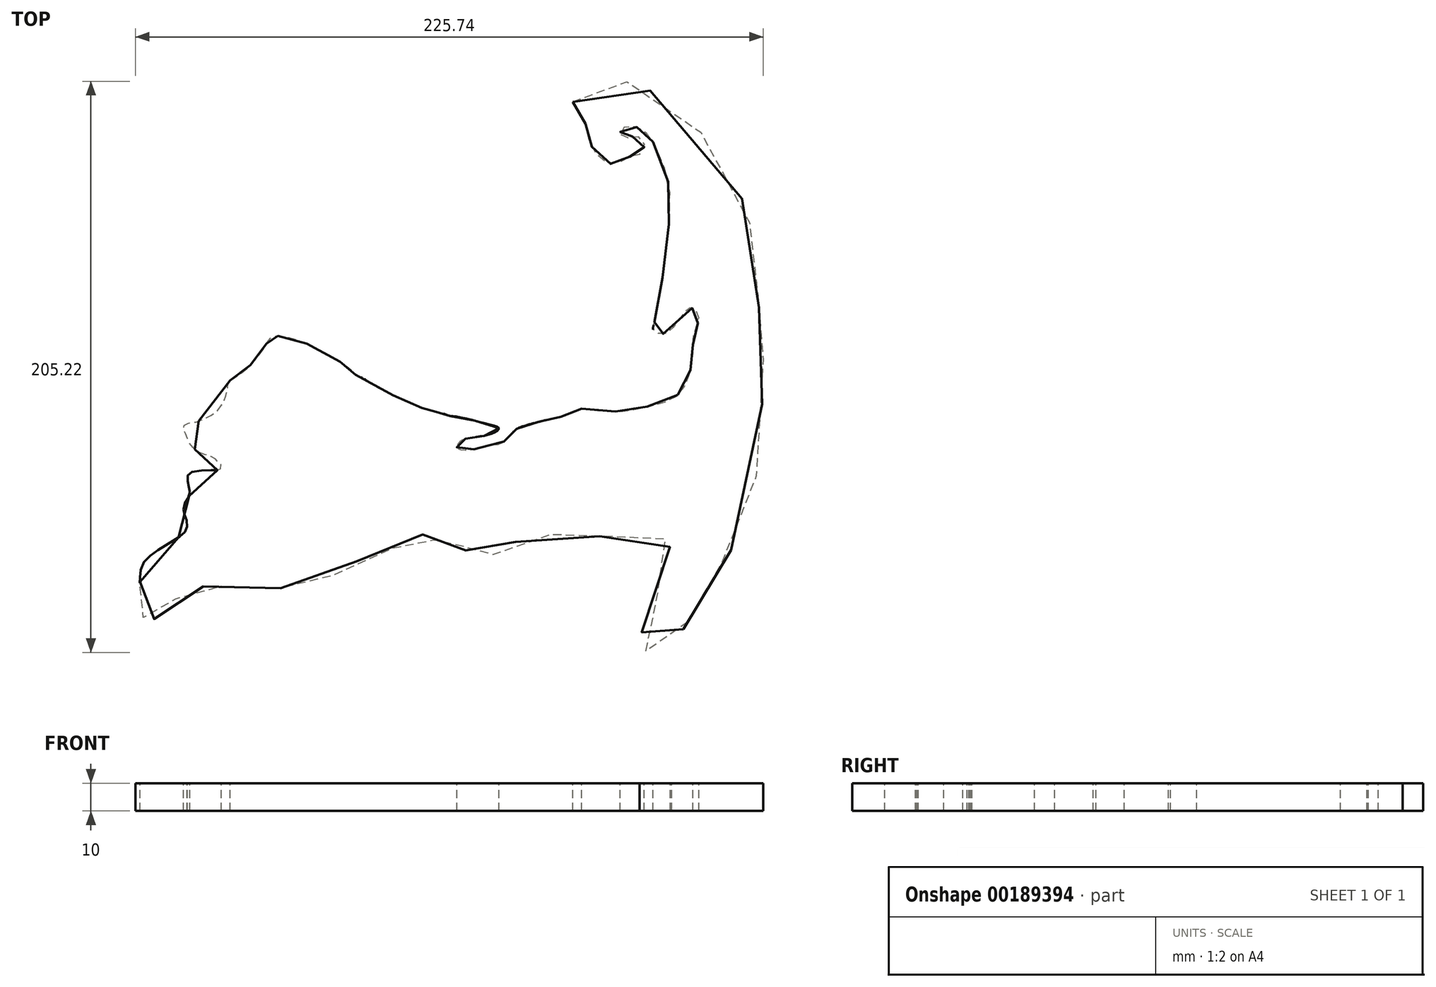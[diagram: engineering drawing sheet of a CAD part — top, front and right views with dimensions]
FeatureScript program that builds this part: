
annotation { "Feature Type Name" : "Feature", "Feature Type Description" : "" }
export const myFeature = defineFeature(function(context is Context, id is Id, definition is map)
    precondition{}
    {
        {
            var Q0;
            Q0=qCreatedBy(makeId("Top.planeOp"),FACE);
            var sketch = newSketch(context, id + "F0", { "sketchPlane" : qUnion([Q0])});
            skLineSegment(sketch, "E0.bottom", {"start": v(114, -114) * mm, "end": v(-114, -114) * mm});
            skLineSegment(sketch, "E0.top", {"start": v(114, 114) * mm, "end": v(-114, 114) * mm});
            skLineSegment(sketch, "E0.left", {"start": v(114, -114) * mm, "end": v(114, 114) * mm});
            skLineSegment(sketch, "E0.right", {"start": v(-114, -114) * mm, "end": v(-114, 114) * mm});
            skPoint(sketch, "E0.middle", {"position": v(0, 0) * mm});
            skSolve(sketch);
        }
        {
            var Q0;
            Q0 = qSketchRegion(id + "F0", true);
            extrude(context, id + "F1", {"entities" : qUnion([Q0]), "depth" : 10 * mm});
        }
        {
            var Q0;
            Q0=makeQuery(id+"F1.opExtrude","CAP_FACE",FACE,{"disambiguationData":[OSD([sQuery(id+"F0.wireOp",EDGE,"E0.bottom"),sQuery(id+"F0.wireOp",EDGE,"E0.top"),sQuery(id+"F0.wireOp",EDGE,"E0.left"),sQuery(id+"F0.wireOp",EDGE,"E0.right")])],"isStart":false});
            var sketch = newSketch(context, id + "F2", { "sketchPlane" : qUnion([Q0])});
            skFitSpline(sketch, "E1", {"points": [v(-78.88, -5.08) * mm, v(-71.93, 0) * mm, v(-65.75, 8.04) * mm, v(-64.34, 10.1) * mm, v(-60.22, 10.76) * mm, v(-45.46, 5.22) * mm, v(-34.6, -2.05) * mm, v(-33.63, -3.24) * mm, v(-31.03, -4.32) * mm, v(-28.86, -5.84) * mm, v(-15.5, -12.68) * mm, v(-8.2, -15.6) * mm, v(-6.75, -15.96) * mm, v(-1.36, -17.33) * mm, v(0, -17.85) * mm, v(1.56, -17.97) * mm, v(14.91, -21.12) * mm, v(17.78, -22.45) * mm, v(15.22, -24.3) * mm, v(8.77, -25.52) * mm, v(5.29, -26.24) * mm, v(3.24, -27.67) * mm, v(2.73, -29.3) * mm, v(5.6, -30.13) * mm, v(11.84, -29.1) * mm, v(13.58, -28.5) * mm, v(15.83, -28.39) * mm, v(19.62, -27.06) * mm, v(23.2, -23.37) * mm, v(26.07, -21.73) * mm, v(36, -19.07) * mm, v(40.82, -18.04) * mm, v(47.56, -15.3) * mm], "startDerivative": vector(166.8, 100.66) * mm, "endDerivative": vector(189.52, 84.83) * mm});
            skFitSpline(sketch, "E2", {"points": [v(47.56, -15.3) * mm, v(57.46, -16.2) * mm, v(64.01, -15.98) * mm, v(73.61, -13.96) * mm, v(81.31, -10.98) * mm, v(85.16, -5.8) * mm, v(86.95, 0) * mm, v(87.53, 5.77) * mm, v(87.53, 9.4) * mm, v(88.54, 13.6) * mm, v(89.7, 16.63) * mm, v(89.12, 19.38) * mm, v(87.38, 20.83) * mm, v(85.65, 20.69) * mm, v(84.05, 18.66) * mm, v(81.3, 15.04) * mm, v(78.55, 12) * mm, v(75.65, 11.7) * mm, v(73.33, 12.72) * mm, v(73.62, 15.62) * mm, v(76.53, 31.15) * mm, v(79.11, 53.37) * mm, v(78.42, 67.32) * mm, v(73.08, 80.75) * mm, v(70.48, 84.05) * mm, v(67.39, 85.9) * mm, v(63.32, 86.06) * mm, v(61.58, 84.97) * mm, v(61.58, 83.24) * mm, v(62.94, 82.15) * mm, v(64.73, 82.31) * mm, v(67.44, 82.58) * mm, v(69.56, 81.23) * mm, v(69.88, 78.24) * mm, v(67.71, 75.7) * mm, v(65.22, 75.42) * mm, v(63.75, 74.61) * mm, v(59.8, 72.77) * mm, v(56.1, 73.3) * mm, v(52.04, 77.21) * mm, v(49.95, 82.77) * mm, v(49.22, 86.1) * mm, v(46.4, 91.9) * mm, v(44.37, 95) * mm], "startDerivative": vector(310, -33.18) * mm, "endDerivative": vector(-90.92, 130.97) * mm});
            skFitSpline(sketch, "E3", {"points": [v(44.37, 95) * mm, v(45.92, 98.47) * mm, v(56.68, 101.95) * mm, v(66.4, 101.65) * mm, v(79.82, 93.66) * mm, v(99.15, 72.93) * mm, v(107.62, 52.53) * mm, v(109.79, 42.33) * mm, v(111.09, 24.46) * mm, v(111.8, 13.57) * mm, v(112.6, 9.88) * mm, v(112.77, 1.47) * mm, v(111.47, -28.99) * mm, v(106, -56.9) * mm, v(97.6, -71.32) * mm, v(91.81, -79.16) * mm, v(86.39, -89.58) * mm, v(82.91, -96.3) * mm, v(77.27, -101.3) * mm, v(72.06, -102.82) * mm, v(68.8, -100.86) * mm, v(68.8, -96.74) * mm, v(73.58, -85.02) * mm, v(78.57, -73.74) * mm, v(79.88, -67.88) * mm, v(77.05, -61.59) * mm, v(70.98, -59.85) * mm, v(65.26, -61.39) * mm, v(58.3, -61.24) * mm, v(44.37, -60.95) * mm, v(39.63, -60.52) * mm, v(32.38, -60.95) * mm, v(22.54, -63.7) * mm, v(15.87, -67.47) * mm, v(14.72, -68.92) * mm, v(11.1, -69.93) * mm, v(7.18, -69.2) * mm, v(5.88, -66.17) * mm, v(4.59, -62.86) * mm, v(2.95, -61.03) * mm, v(-0.8, -62.22) * mm, v(-3.44, -63.13) * mm, v(-7.18, -61.58) * mm, v(-13.3, -60.3) * mm, v(-18.95, -63.95) * mm, v(-20.32, -65.41) * mm, v(-27.64, -67.35) * mm, v(-36.39, -71.95) * mm, v(-46.67, -77.78) * mm, v(-53.88, -79.93) * mm, v(-59.4, -79.63) * mm, v(-63.4, -80.09) * mm, v(-70.3, -79.32) * mm, v(-79.81, -79.17) * mm, v(-88, -79.15) * mm, v(-90.9, -79.84) * mm, v(-95.43, -81.9) * mm, v(-100.57, -85.28) * mm, v(-103.95, -88.89) * mm, v(-105.8, -90.65) * mm, v(-108.17, -91.11) * mm, v(-111.09, -89.58) * mm, v(-112.7, -87.35) * mm, v(-112.7, -83.29) * mm, v(-111.78, -79.07) * mm, v(-111.32, -77.84) * mm, v(-111.24, -75.54) * mm, v(-110.32, -71.17) * mm, v(-106.07, -66.97) * mm, v(-101.36, -63.93) * mm, v(-97.05, -61.28) * mm, v(-94.8, -59.04) * mm, v(-94.35, -56.74) * mm, v(-94.92, -53.98) * mm, v(-95.61, -52.09) * mm, v(-95.1, -49.1) * mm, v(-93.84, -47.19) * mm, v(-93.39, -44.41) * mm, v(-93.97, -42.54) * mm, v(-94.16, -40.16) * mm, v(-93.52, -38.41) * mm, v(-87.65, -37.45) * mm, v(-83.71, -37.38) * mm, v(-82.74, -37.25) * mm, v(-81.97, -36.16) * mm, v(-82.49, -34.87) * mm, v(-83.45, -34.22) * mm, v(-84.16, -33.38) * mm, v(-86.1, -32.22) * mm, v(-88.61, -31.58) * mm, v(-91.32, -30.03) * mm, v(-93.65, -27.45) * mm, v(-94.1, -26.1) * mm, v(-94.74, -24.54) * mm, v(-95.52, -23.25) * mm, v(-95.52, -21.7) * mm, v(-94.68, -20.67) * mm, v(-91.34, -20.1) * mm, v(-86.68, -18.25) * mm, v(-82.95, -15.55) * mm, v(-80.36, -10.72) * mm, v(-79.69, -7.26) * mm, v(-79.52, -5.8) * mm, v(-78.88, -5.08) * mm], "startDerivative": vector(72.46, 444.16) * mm, "endDerivative": vector(185.1, 153.17) * mm});
            skLineSegment(sketch, "E4.bottom", {"start": v(135, -135) * mm, "end": v(-135, -135) * mm});
            skLineSegment(sketch, "E4.top", {"start": v(135, 135) * mm, "end": v(-135, 135) * mm});
            skLineSegment(sketch, "E4.left", {"start": v(135, -135) * mm, "end": v(135, 135) * mm});
            skLineSegment(sketch, "E4.right", {"start": v(-135, -135) * mm, "end": v(-135, 135) * mm});
            skPoint(sketch, "E4.middle", {"position": v(0, 0) * mm});
            skSolve(sketch);
        }
        {
            var Q0;
            Q0 = qSketchRegion(id + "F2", true);
            extrude(context, id + "F3", {"entities" : qUnion([Q0]), "operationType" : NewBodyOperationType.REMOVE, "endBound" : BoundingType.THROUGH_ALL, "oppositeDirection" : true, "depth" : 25 * mm});
        }
    });
